# Revit family: 0043565 Feilo Sylvania Lighting Fixture SKYLINE LED MINI 10K SYM WHITE
name_source: partatom
category: Lighting Fixtures
revit_build: Autodesk Revit 2017 (Build: 20190507_1515(x64)
units: mm (PartAtom-declared; Revit-internal decimal feet)

## family parameters
Cut with Voids When Loaded = No
Host = Face
Light Source = No
OmniClass Number = 23.80.70.00
OmniClass Title = Lighting
Part Type = Normal
Room Calculation Point = No
Round Connector Dimension = Use Diameter
Shared = No

## types (1)
- 0043565 SKYLINE LED MINI 10K SYM WHITE
    Apparent Load = 74 VA
    Assembly Code = D5020200
    AssetType = Fixed
    ClassificationName = Uniclass2015
    ClassificationValue = EF_70_80
    Cost = 0 $
    Default Elevation = 1219 mm
    Description = Exterior LED Pole top luminaire, comes complete with a 6m cable, light weight and compact, Aluminium housing,  White - RAL9003, Symmetrical distribution, IP65, IK08, CLASS I, 4000K, non dimming, 10.444 lm, 74W, 141lm/W, driver current 500mA, CRI70, 76,000hrs L70B50 lifetime, Ø484x352mm - 6.65kg, 5 step MacAdam ellipse, suitable for 76mm pole tops
    DimmingControlOptions = Non dimmable
    DocumentationLiterature = http://www.sylvania-lighting.com
    DurationUnit = hours
    ElectricShockClassification = Class I
    ExpectedLife = 50000
    IfcExportAs = IfcLightFixtureType
    IfcExportType = IfcLightFixtureType
    ImpactProtectionIndex = IK08
    IngressProtection = IP65
    InputNominalFrequency = 50/60 Hz
    InputVoltage = 230-240V~
    Keynote = 16500
    Lamp = LED
    LampColourRenderingIndex = 70
    LampColourTemperature = 4000 K
    LampMacAdamStep = 5
    LampNominalLuminous = 10444 lm
    LampsType = LED
    LightOutputRatio = 100
    LuminousEfficacy = 141 lm/W
    Manufacturer = Feilo Sylvania
    ManufacturerName = Feilo Sylvania
    Material = aluminium housing
    Material_1_FEILO = <By Category>
    Material_2_FEILO = <By Category>
    Material_3_FEILO = <By Category>
    Material_4_FEILO = <By Category>
    Model = SKYLINE LED MINI 10K SYM WHITE
    ModelNumber = 0043565
    ModelReference = SKYLINE LED MINI 10K SYM WHITE
    Name = SKYLINE LED MINI 10K SYM WHITE
    NominalDepth = 484 mm
    NominalHeight = 352 mm
    NominalLength = 0 mm  [stored 0 ft]
    PowerConsumption = 74 W
    PowerFactor = 0.98
    Type Image = <None>
    TypeName = SKYLINE LED MINI 10K SYM WHITE
    URL = http://www.sylvania-lighting.com
    Voltage = 230 V
    Weight = 6.65 kg

note: [stored X ft] marks values corroborated as IEEE doubles in the binary element streams (Revit-internal decimal feet)

## geometry (parser evidence)
native form markers: Sweep x6
no freeform markers — native parametric forms only
